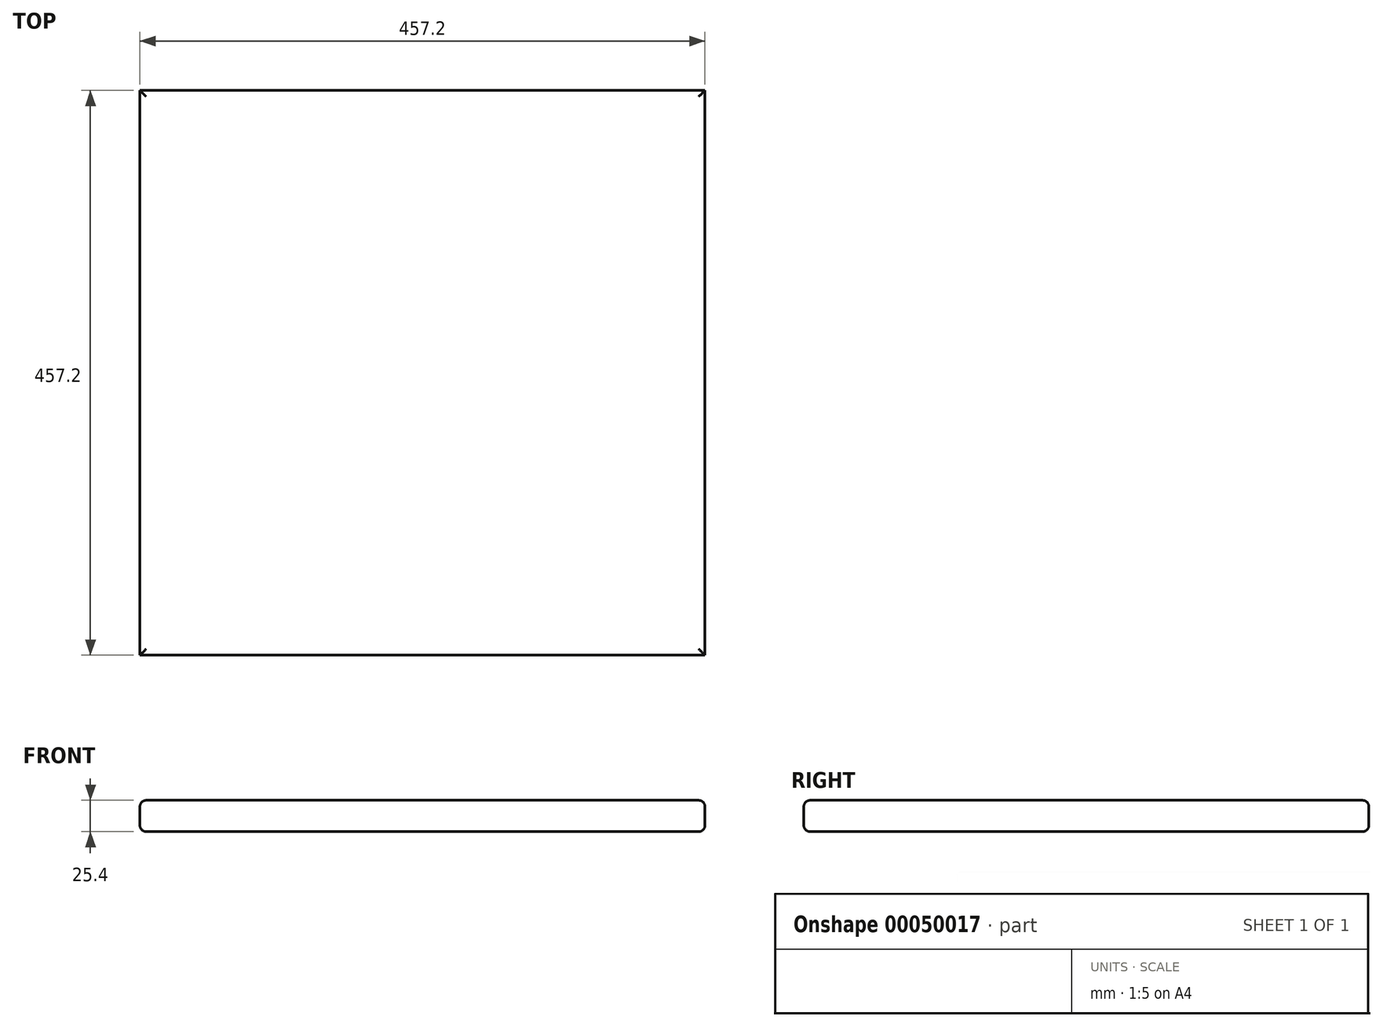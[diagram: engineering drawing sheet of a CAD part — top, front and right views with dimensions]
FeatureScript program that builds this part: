
annotation { "Feature Type Name" : "Feature", "Feature Type Description" : "" }
export const myFeature = defineFeature(function(context is Context, id is Id, definition is map)
    precondition{}
    {
        {
            var Q0;
            Q0=qCreatedBy(makeId("Top.planeOp"),FACE);
            var sketch = newSketch(context, id + "F0", { "sketchPlane" : qUnion([Q0])});
            skLineSegment(sketch, "E0.bottom", {"start": v(0, 0) * mm, "end": v(457.2, 0) * mm});
            skLineSegment(sketch, "E0.top", {"start": v(0, -457.2) * mm, "end": v(457.2, -457.2) * mm});
            skLineSegment(sketch, "E0.left", {"start": v(0, 0) * mm, "end": v(0, -457.2) * mm});
            skLineSegment(sketch, "E0.right", {"start": v(457.2, 0) * mm, "end": v(457.2, -457.2) * mm});
            skSolve(sketch);
        }
        {
            var Q0;
            Q0=makeQuery(id+"F0.imprint","IMPRINT",FACE,{"disambiguationData":[TD([[makeQuery(id+"F0.imprint","IMPRINT",EDGE,{"derivedFrom":sQuery(id+"F0.wireOp",EDGE,"E0.bottom")}),-1.0]])]});
            extrude(context, id + "F1", {"entities" : qUnion([Q0]), "depth" : 25.4 * mm});
        }
        {
            var Q0;
            Q0=makeQuery(id+"F1.opExtrude","CAP_EDGE",EDGE,{"disambiguationData":[OSD([sQuery(id+"F0.wireOp",EDGE,"E0.left")])],"isStart":false});
            var Q1;
            Q1=makeQuery(id+"F1.opExtrude","CAP_EDGE",EDGE,{"disambiguationData":[OSD([sQuery(id+"F0.wireOp",EDGE,"E0.bottom")])],"isStart":false});
            var Q2;
            Q2=makeQuery(id+"F1.opExtrude","CAP_EDGE",EDGE,{"disambiguationData":[OSD([sQuery(id+"F0.wireOp",EDGE,"E0.right")])],"isStart":false});
            var Q3;
            Q3=makeQuery(id+"F1.opExtrude","CAP_EDGE",EDGE,{"disambiguationData":[OSD([sQuery(id+"F0.wireOp",EDGE,"E0.top")])],"isStart":false});
            var Q4;
            Q4=makeQuery(id+"F1.opExtrude","CAP_EDGE",EDGE,{"disambiguationData":[OSD([sQuery(id+"F0.wireOp",EDGE,"E0.top")])],"isStart":true});
            var Q5;
            Q5=makeQuery(id+"F1.opExtrude","CAP_EDGE",EDGE,{"disambiguationData":[OSD([sQuery(id+"F0.wireOp",EDGE,"E0.right")])],"isStart":true});
            var Q6;
            Q6=makeQuery(id+"F1.opExtrude","CAP_EDGE",EDGE,{"disambiguationData":[OSD([sQuery(id+"F0.wireOp",EDGE,"E0.left")])],"isStart":true});
            var Q7;
            Q7=makeQuery(id+"F1.opExtrude","CAP_EDGE",EDGE,{"disambiguationData":[OSD([sQuery(id+"F0.wireOp",EDGE,"E0.bottom")])],"isStart":true});
            fillet(context, id + "F2", {"entities" : qUnion([Q0, Q1, Q2, Q3, Q4, Q5, Q6, Q7]), "radius" : 5.08 * mm, "tangentPropagation" : true, "allowEdgeOverflow" : false});
        }
    });
